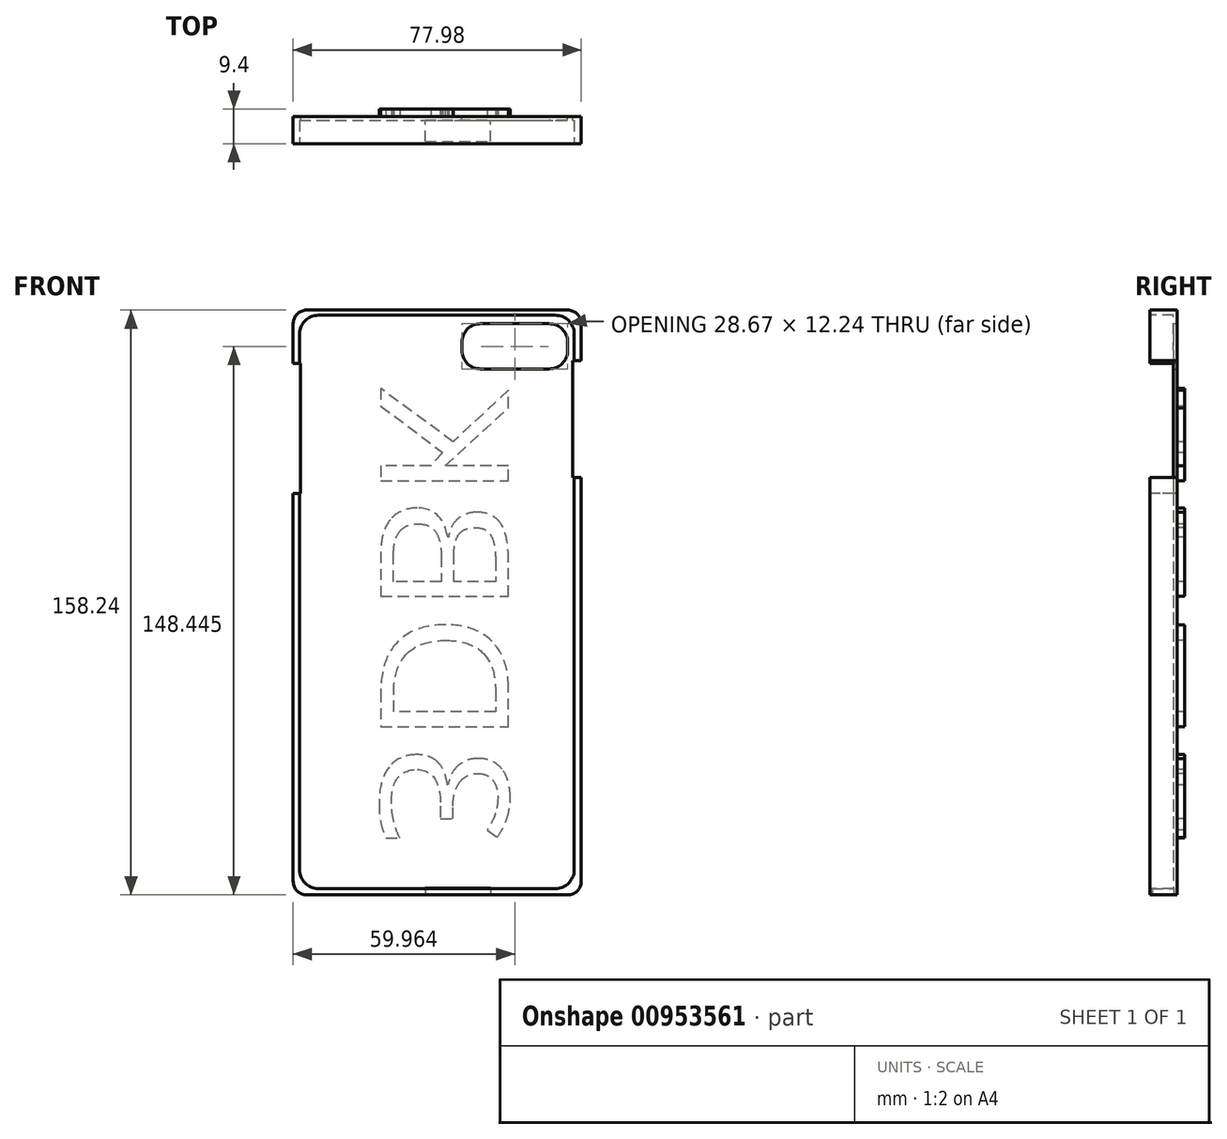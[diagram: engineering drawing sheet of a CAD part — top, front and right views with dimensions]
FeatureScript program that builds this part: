
annotation { "Feature Type Name" : "Feature", "Feature Type Description" : "" }
export const myFeature = defineFeature(function(context is Context, id is Id, definition is map)
    precondition{}
    {
        {
            var Q0;
            Q0=qCreatedBy(makeId("Front.planeOp"),FACE);
            var sketch = newSketch(context, id + "F0", { "sketchPlane" : qUnion([Q0])});
            skLineSegment(sketch, "E0", {"start": v(32.35, 87.47) * mm, "end": v(32.35, -70.77) * mm});
            skLineSegment(sketch, "E1", {"start": v(32.35, -70.77) * mm, "end": v(-45.63, -70.77) * mm});
            skLineSegment(sketch, "E2", {"start": v(-45.63, -70.77) * mm, "end": v(-45.63, 87.47) * mm});
            skLineSegment(sketch, "E3", {"start": v(-45.63, 87.47) * mm, "end": v(32.35, 87.47) * mm});
            skSolve(sketch);
        }
        {
            var Q0;
            Q0 = qSketchRegion(id + "F0", true);
            extrude(context, id + "F1", {"entities" : qUnion([Q0]), "depth" : 7.37 * mm, "offsetDistance" : 25.4 * mm});
        }
        {
            var Q0;
            Q0=makeQuery(id+"F1.opExtrude","CAP_FACE",FACE,{"disambiguationData":[OSD([sQuery(id+"F0.wireOp",EDGE,"E0"),sQuery(id+"F0.wireOp",EDGE,"E1"),sQuery(id+"F0.wireOp",EDGE,"E2"),sQuery(id+"F0.wireOp",EDGE,"E3")])],"isStart":false});
            var sketch = newSketch(context, id + "F2", { "sketchPlane" : qUnion([Q0])});
            skSolve(sketch);
        }
        {
            var Q0;
            Q0=makeQuery(id+"F2.imprint","IMPRINT",FACE,{"disambiguationData":[TD([[makeQuery(id+"F2.imprint","IMPRINT",EDGE,{"derivedFrom":makeQuery(id+"F1.opExtrude","CAP_EDGE",EDGE,{"disambiguationData":[OSD([sQuery(id+"F0.wireOp",EDGE,"E0")])],"isStart":false})}),-1.0]])]});
            var sketch = newSketch(context, id + "F3", { "sketchPlane" : qUnion([Q0])});
            skLineSegment(sketch, "E4.bottom", {"start": v(-43.88, 86.08) * mm, "end": v(30.43, 86.08) * mm});
            skLineSegment(sketch, "E4.top", {"start": v(-43.88, -69.05) * mm, "end": v(30.43, -69.05) * mm});
            skLineSegment(sketch, "E4.left", {"start": v(-43.88, 86.08) * mm, "end": v(-43.88, -69.05) * mm});
            skLineSegment(sketch, "E4.right", {"start": v(30.43, 86.08) * mm, "end": v(30.43, -69.05) * mm});
            skSolve(sketch);
        }
        {
            var Q0;
            Q0 = qSketchRegion(id + "F3", true);
            extrude(context, id + "F4", {"entities" : qUnion([Q0]), "operationType" : NewBodyOperationType.REMOVE, "oppositeDirection" : true, "depth" : 6.35 * mm, "offsetDistance" : 25.4 * mm});
        }
        {
            var Q0;
            Q0=makeQuery(id+"F1.opExtrude","SWEPT_EDGE",EDGE,{"disambiguationData":[OSD([sQuery(id+"F0.wireOp",EDGE,"E0"),sQuery(id+"F0.wireOp",EDGE,"E3")])]});
            fillet(context, id + "F5", {"entities" : qUnion([Q0]), "radius" : 3.68 * mm, "tangentPropagation" : true, "allowEdgeOverflow" : false});
        }
        {
            var Q0;
            Q0=makeQuery(id+"F1.opExtrude","SWEPT_EDGE",EDGE,{"disambiguationData":[OSD([sQuery(id+"F0.wireOp",EDGE,"E0"),sQuery(id+"F0.wireOp",EDGE,"E1")])]});
            var Q1;
            Q1=makeQuery(id+"F1.opExtrude","SWEPT_EDGE",EDGE,{"disambiguationData":[OSD([sQuery(id+"F0.wireOp",EDGE,"E1"),sQuery(id+"F0.wireOp",EDGE,"E2")])]});
            var Q2;
            Q2=makeQuery(id+"F1.opExtrude","SWEPT_EDGE",EDGE,{"disambiguationData":[OSD([sQuery(id+"F0.wireOp",EDGE,"E2"),sQuery(id+"F0.wireOp",EDGE,"E3")])]});
            fillet(context, id + "F6", {"entities" : qUnion([Q0, Q1, Q2]), "radius" : 3.68 * mm, "tangentPropagation" : true, "allowEdgeOverflow" : false});
        }
        {
            var Q0;
            Q0=makeQuery(id+"F4.boolean.opBoolean","COPY",EDGE,{"derivedFrom":makeQuery(id+"F4.opExtrude","SWEPT_EDGE",EDGE,{"disambiguationData":[OSD([sQuery(id+"F3.wireOp",EDGE,"E4.bottom"),sQuery(id+"F3.wireOp",EDGE,"E4.left")])]})});
            var Q1;
            Q1=makeQuery(id+"F4.boolean.opBoolean","COPY",EDGE,{"derivedFrom":makeQuery(id+"F4.opExtrude","SWEPT_EDGE",EDGE,{"disambiguationData":[OSD([sQuery(id+"F3.wireOp",EDGE,"E4.bottom"),sQuery(id+"F3.wireOp",EDGE,"E4.right")])]})});
            var Q2;
            Q2=makeQuery(id+"F4.boolean.opBoolean","COPY",EDGE,{"derivedFrom":makeQuery(id+"F4.opExtrude","SWEPT_EDGE",EDGE,{"disambiguationData":[OSD([sQuery(id+"F3.wireOp",EDGE,"E4.top"),sQuery(id+"F3.wireOp",EDGE,"E4.left")])]})});
            var Q3;
            Q3=makeQuery(id+"F4.boolean.opBoolean","COPY",EDGE,{"derivedFrom":makeQuery(id+"F4.opExtrude","SWEPT_EDGE",EDGE,{"disambiguationData":[OSD([sQuery(id+"F3.wireOp",EDGE,"E4.top"),sQuery(id+"F3.wireOp",EDGE,"E4.right")])]})});
            fillet(context, id + "F7", {"entities" : qUnion([Q0, Q1, Q2, Q3]), "radius" : 5.08 * mm, "tangentPropagation" : true, "allowEdgeOverflow" : false});
        }
        {
            var Q0;
            Q0=makeQuery(id+"F1.opExtrude","SWEPT_FACE",FACE,{"disambiguationData":[OSD([sQuery(id+"F0.wireOp",EDGE,"E1")])]});
            var sketch = newSketch(context, id + "F8", { "sketchPlane" : qUnion([Q0])});
            skLineSegment(sketch, "E5.bottom", {"start": v(-9.92, 6.78) * mm, "end": v(7.84, 6.78) * mm});
            skLineSegment(sketch, "E5.top", {"start": v(-9.92, 0.94) * mm, "end": v(7.84, 0.94) * mm});
            skLineSegment(sketch, "E5.left", {"start": v(-9.92, 6.78) * mm, "end": v(-9.92, 0.94) * mm});
            skLineSegment(sketch, "E5.right", {"start": v(7.84, 6.78) * mm, "end": v(7.84, 0.94) * mm});
            skSolve(sketch);
        }
        {
            var Q0;
            Q0=makeQuery(id+"F8.imprint","IMPRINT",FACE,{"disambiguationData":[TD([[makeQuery(id+"F8.imprint","IMPRINT",EDGE,{"derivedFrom":sQuery(id+"F8.wireOp",EDGE,"E5.bottom")}),-1.0]])]});
            extrude(context, id + "F9", {"entities" : qUnion([Q0]), "operationType" : NewBodyOperationType.REMOVE, "oppositeDirection" : true, "depth" : 1.8 * mm, "offsetDistance" : 25.4 * mm});
        }
        {
            var Q0;
            Q0=makeQuery(id+"F1.opExtrude","CAP_FACE",FACE,{"disambiguationData":[OSD([sQuery(id+"F0.wireOp",EDGE,"E0"),sQuery(id+"F0.wireOp",EDGE,"E1"),sQuery(id+"F0.wireOp",EDGE,"E2"),sQuery(id+"F0.wireOp",EDGE,"E3")])],"isStart":true});
            var sketch = newSketch(context, id + "F10", { "sketchPlane" : qUnion([Q0])});
            skLineSegment(sketch, "E6.bottom", {"start": v(-28.67, 83.8) * mm, "end": v(0, 83.8) * mm});
            skLineSegment(sketch, "E6.top", {"start": v(-28.67, 71.56) * mm, "end": v(0, 71.56) * mm});
            skLineSegment(sketch, "E6.left", {"start": v(-28.67, 83.8) * mm, "end": v(-28.67, 71.56) * mm});
            skLineSegment(sketch, "E6.right", {"start": v(0, 83.8) * mm, "end": v(0, 71.56) * mm});
            skSolve(sketch);
        }
        {
            var Q0;
            Q0=makeQuery(id+"F10.imprint","IMPRINT",FACE,{"disambiguationData":[TD([[makeQuery(id+"F10.imprint","IMPRINT",EDGE,{"derivedFrom":sQuery(id+"F10.wireOp",EDGE,"E6.bottom")}),1.0]])]});
            var sketch = newSketch(context, id + "F11", { "sketchPlane" : qUnion([Q0])});
            skSolve(sketch);
        }
        {
            var Q0;
            Q0 = qSketchRegion(id + "F11", true);
            var Q1;
            Q1=makeQuery(id+"F10.imprint","IMPRINT",FACE,{"disambiguationData":[TD([[makeQuery(id+"F10.imprint","IMPRINT",EDGE,{"derivedFrom":sQuery(id+"F10.wireOp",EDGE,"E6.bottom")}),-1.0]])]});
            extrude(context, id + "F12", {"entities" : qUnion([Q0, Q1]), "operationType" : NewBodyOperationType.REMOVE, "oppositeDirection" : true, "depth" : 25.4 * mm, "offsetDistance" : 25.4 * mm});
        }
        {
            var Q0;
            Q0=makeQuery(id+"F12.boolean.opBoolean","COPY",EDGE,{"derivedFrom":makeQuery(id+"F12.opExtrude","SWEPT_EDGE",EDGE,{"disambiguationData":[OSD([sQuery(id+"F10.wireOp",EDGE,"E6.bottom"),sQuery(id+"F10.wireOp",EDGE,"E6.right")])]})});
            var Q1;
            Q1=makeQuery(id+"F12.boolean.opBoolean","COPY",EDGE,{"derivedFrom":makeQuery(id+"F12.opExtrude","SWEPT_EDGE",EDGE,{"disambiguationData":[OSD([sQuery(id+"F10.wireOp",EDGE,"E6.top"),sQuery(id+"F10.wireOp",EDGE,"E6.left")])]})});
            var Q2;
            Q2=makeQuery(id+"F12.boolean.opBoolean","COPY",EDGE,{"derivedFrom":makeQuery(id+"F12.opExtrude","SWEPT_EDGE",EDGE,{"disambiguationData":[OSD([sQuery(id+"F10.wireOp",EDGE,"E6.bottom"),sQuery(id+"F10.wireOp",EDGE,"E6.left")])]})});
            var Q3;
            Q3=makeQuery(id+"F12.boolean.opBoolean","COPY",EDGE,{"derivedFrom":makeQuery(id+"F12.opExtrude","SWEPT_EDGE",EDGE,{"disambiguationData":[OSD([sQuery(id+"F10.wireOp",EDGE,"E6.top"),sQuery(id+"F10.wireOp",EDGE,"E6.right")])]})});
            fillet(context, id + "F13", {"entities" : qUnion([Q0, Q1, Q2, Q3]), "radius" : 5.08 * mm, "tangentPropagation" : true, "allowEdgeOverflow" : false});
        }
        {
            var Q0;
            Q0=makeQuery(id+"F1.opExtrude","SWEPT_FACE",FACE,{"disambiguationData":[OSD([sQuery(id+"F0.wireOp",EDGE,"E0")])]});
            var sketch = newSketch(context, id + "F14", { "sketchPlane" : qUnion([Q0])});
            skLineSegment(sketch, "E7.bottom", {"start": v(-7.37, 73.86) * mm, "end": v(0, 73.86) * mm});
            skLineSegment(sketch, "E7.top", {"start": v(-7.37, 42.14) * mm, "end": v(0, 42.14) * mm});
            skLineSegment(sketch, "E7.left", {"start": v(-7.37, 73.86) * mm, "end": v(-7.37, 42.14) * mm});
            skLineSegment(sketch, "E7.right", {"start": v(0, 73.86) * mm, "end": v(0, 42.14) * mm});
            skSolve(sketch);
        }
        {
            var Q0;
            Q0 = qSketchRegion(id + "F14", true);
            extrude(context, id + "F15", {"entities" : qUnion([Q0]), "operationType" : NewBodyOperationType.REMOVE, "oppositeDirection" : true, "depth" : 2.3 * mm, "offsetDistance" : 25.4 * mm});
        }
        {
            var Q0;
            Q0=makeQuery(id+"F1.opExtrude","SWEPT_FACE",FACE,{"disambiguationData":[OSD([sQuery(id+"F0.wireOp",EDGE,"E2")])]});
            var sketch = newSketch(context, id + "F16", { "sketchPlane" : qUnion([Q0])});
            skLineSegment(sketch, "E8.bottom", {"start": v(0, 73.1) * mm, "end": v(7.37, 73.1) * mm});
            skLineSegment(sketch, "E8.top", {"start": v(0, 37.9) * mm, "end": v(7.37, 37.9) * mm});
            skLineSegment(sketch, "E8.left", {"start": v(0, 73.1) * mm, "end": v(0, 37.9) * mm});
            skLineSegment(sketch, "E8.right", {"start": v(7.37, 73.1) * mm, "end": v(7.37, 37.9) * mm});
            skSolve(sketch);
        }
        {
            var Q0;
            Q0=makeQuery(id+"F16.imprint","IMPRINT",FACE,{"disambiguationData":[TD([[makeQuery(id+"F16.imprint","IMPRINT",EDGE,{"derivedFrom":sQuery(id+"F16.wireOp",EDGE,"E8.bottom")}),-1.0]])]});
            extrude(context, id + "F17", {"entities" : qUnion([Q0]), "operationType" : NewBodyOperationType.REMOVE, "oppositeDirection" : true, "depth" : 2.03 * mm, "offsetDistance" : 25.4 * mm});
        }
        {
            var Q0;
            Q0=makeQuery(id+"F11.imprint","IMPRINT",FACE,{"disambiguationData":[TD([[makeQuery(id+"F11.imprint","IMPRINT",EDGE,{"derivedFrom":makeQuery(id+"F10.imprint","IMPRINT",EDGE,{"derivedFrom":sQuery(id+"F10.wireOp",EDGE,"E6.bottom")})}),1.0]])]});
            var sketch = newSketch(context, id + "F18", { "sketchPlane" : qUnion([Q0])});
            skText(sketch, "E9", { "text": "3DBK\n", "fontName": "OpenSans-Regular.ttf"});
            const initialGuessF18  = {"E9": [0.0219, -0.05759, 0, 1, 0.0348]};
            skSetInitialGuess(sketch, initialGuessF18);
            skSolve(sketch);
        }
        {
            var Q0;
            Q0 = qSketchRegion(id + "F18", true);
            extrude(context, id + "F19", {"entities" : qUnion([Q0]), "operationType" : NewBodyOperationType.ADD, "depth" : 2.03 * mm, "offsetDistance" : 25.4 * mm});
        }
    });
